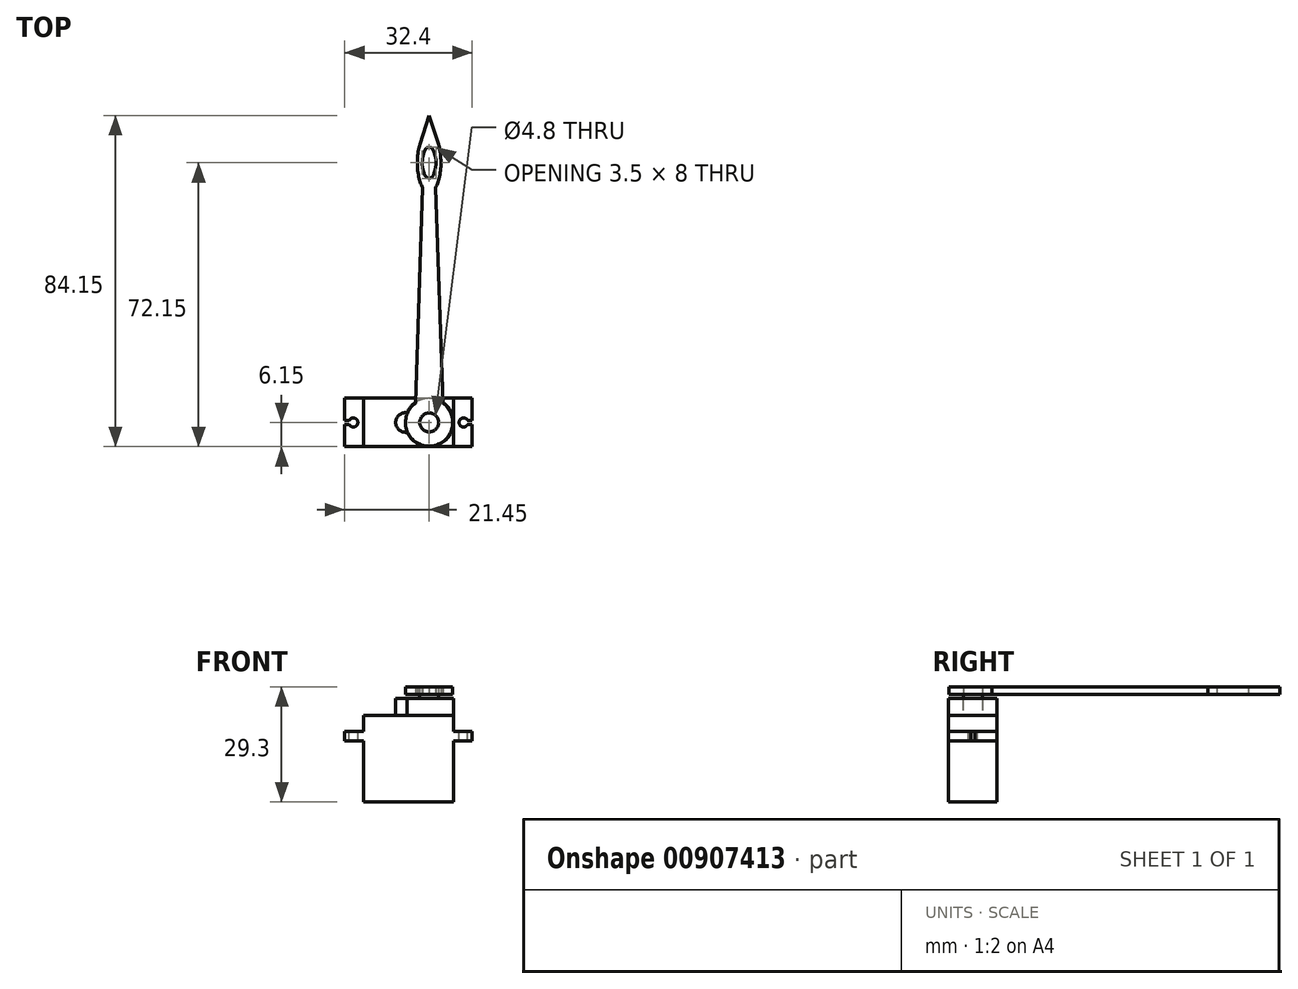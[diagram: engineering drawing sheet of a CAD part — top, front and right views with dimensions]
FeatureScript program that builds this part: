
annotation { "Feature Type Name" : "Feature", "Feature Type Description" : "" }
export const myFeature = defineFeature(function(context is Context, id is Id, definition is map)
    precondition{}
    {
        {
            var Q0;
            Q0=qCreatedBy(makeId("Top.planeOp"),FACE);
            var sketch = newSketch(context, id + "F0", { "sketchPlane" : qUnion([Q0])});
            skLineSegment(sketch, "E0.bottom", {"start": v(0, 0) * mm, "end": v(22.8, 0) * mm});
            skLineSegment(sketch, "E0.top", {"start": v(0, 12.3) * mm, "end": v(22.8, 12.3) * mm});
            skLineSegment(sketch, "E0.left", {"start": v(0, 0) * mm, "end": v(0, 12.3) * mm});
            skLineSegment(sketch, "E0.right", {"start": v(22.8, 0) * mm, "end": v(22.8, 12.3) * mm});
            skSolve(sketch);
        }
        {
            var Q0;
            Q0=qSketchRegion(id+"F0",true);
            extrude(context, id + "F1", {"entities" : qUnion([Q0]), "depth" : 18 * mm, "offsetDistance" : 25 * mm});
        }
        {
            var Q0;
            Q0=makeQuery(id+"F1.opExtrude","CAP_FACE",FACE,{"disambiguationData":[OSD([sQuery(id+"F0.wireOp",EDGE,"E0.bottom"),sQuery(id+"F0.wireOp",EDGE,"E0.top"),sQuery(id+"F0.wireOp",EDGE,"E0.left"),sQuery(id+"F0.wireOp",EDGE,"E0.right")])],"isStart":false});
            var sketch = newSketch(context, id + "F2", { "sketchPlane" : qUnion([Q0])});
            skLineSegment(sketch, "E1.0", {"start": v(0, 12.3) * mm, "end": v(22.8, 12.3) * mm});
            skLineSegment(sketch, "E2.0", {"start": v(0, 0) * mm, "end": v(22.8, 0) * mm});
            skLineSegment(sketch, "E3", {"start": v(0, 12.3) * mm, "end": v(-4.8, 12.3) * mm});
            skLineSegment(sketch, "E4", {"start": v(-4.8, 12.3) * mm, "end": v(-4.8, 6.65) * mm});
            skLineSegment(sketch, "E5", {"start": v(-4.8, 0) * mm, "end": v(0, 0) * mm});
            skLineSegment(sketch, "E6", {"start": v(22.8, 0) * mm, "end": v(27.6, 0) * mm});
            skLineSegment(sketch, "E7", {"start": v(27.6, 0) * mm, "end": v(27.6, 5.65) * mm});
            skLineSegment(sketch, "E8", {"start": v(27.6, 12.3) * mm, "end": v(22.8, 12.3) * mm});
            skArc(sketch, "E9", {"start": v(-3.64, 5.65) * mm, "mid": v(-1.45, 6.15) * mm, "end": v(-3.64, 6.65) * mm});
            skArc(sketch, "E10", {"start": v(26.44, 6.65) * mm, "mid": v(24.25, 6.15) * mm, "end": v(26.44, 5.65) * mm});
            skPoint(sketch, "E10.centerSnap0", {"position": v(22.8, 6.15) * mm});
            skLineSegment(sketch, "E11", {"start": v(-2.6, 6.15) * mm, "end": v(25.4, 6.15) * mm, "construction": true});
            skLineSegment(sketch, "E12", {"start": v(11.4, 6.15) * mm, "end": v(11.4, 12.3) * mm, "construction": true});
            skLineSegment(sketch, "E13", {"start": v(-4.8, 6.65) * mm, "end": v(-3.64, 6.65) * mm});
            skLineSegment(sketch, "E14", {"start": v(-4.8, 5.65) * mm, "end": v(-3.64, 5.65) * mm});
            skLineSegment(sketch, "E15", {"start": v(26.44, 6.65) * mm, "end": v(27.6, 6.65) * mm});
            skLineSegment(sketch, "E16", {"start": v(26.44, 5.65) * mm, "end": v(27.6, 5.65) * mm});
            skLineSegment(sketch, "E17.trimOffspring", {"start": v(-4.8, 5.65) * mm, "end": v(-4.8, 0) * mm});
            skLineSegment(sketch, "E18.trimOffspring", {"start": v(27.6, 6.65) * mm, "end": v(27.6, 12.3) * mm});
            skSolve(sketch);
        }
        {
            var Q0;
            Q0=qSketchRegion(id+"F2",true);
            extrude(context, id + "F3", {"entities" : qUnion([Q0]), "operationType" : NewBodyOperationType.ADD, "oppositeDirection" : true, "depth" : 2.5 * mm, "offsetDistance" : 25 * mm});
        }
        {
            var Q0;
            Q0=makeQuery(id+"F3.boolean.opBoolean","MERGE",FACE,{"derivedFrom":[makeQuery(id+"F1.opExtrude","CAP_FACE",FACE,{"disambiguationData":[OSD([sQuery(id+"F0.wireOp",EDGE,"E0.bottom"),sQuery(id+"F0.wireOp",EDGE,"E0.top"),sQuery(id+"F0.wireOp",EDGE,"E0.left"),sQuery(id+"F0.wireOp",EDGE,"E0.right")])],"isStart":false}),makeQuery(id+"F3.opExtrude","CAP_FACE",FACE,{"disambiguationData":[OSD([sQuery(id+"F2.wireOp",EDGE,"E1.0"),sQuery(id+"F2.wireOp",EDGE,"E2.0"),sQuery(id+"F2.wireOp",EDGE,"E3"),sQuery(id+"F2.wireOp",EDGE,"E4"),sQuery(id+"F2.wireOp",EDGE,"E5"),sQuery(id+"F2.wireOp",EDGE,"E6"),sQuery(id+"F2.wireOp",EDGE,"E7"),sQuery(id+"F2.wireOp",EDGE,"E8"),sQuery(id+"F2.wireOp",EDGE,"E9"),sQuery(id+"F2.wireOp",EDGE,"E10")])],"isStart":true})]});
            var sketch = newSketch(context, id + "F4", { "sketchPlane" : qUnion([Q0])});
            skLineSegment(sketch, "E19.0", {"start": v(22.8, 0) * mm, "end": v(22.8, 12.3) * mm});
            skLineSegment(sketch, "E20.0", {"start": v(0, 0) * mm, "end": v(0, 12.3) * mm});
            skSolve(sketch);
        }
        {
            var Q0;
            {var subQ0=sQuery(id+"F4.wireOp",EDGE,"E19.0");Q0=makeQuery(id+"F4.imprint","IMPRINT",FACE,{"disambiguationData":[TD([[makeQuery(id+"F4.imprint","IMPRINT",EDGE,{"derivedFrom":subQ0}),1.0]])]});}
            extrude(context, id + "F5", {"entities" : qUnion([Q0]), "operationType" : NewBodyOperationType.ADD, "depth" : 4 * mm, "offsetDistance" : 25 * mm});
        }
        {
            var Q0;
            Q0=makeQuery(id+"F5.opExtrude","CAP_FACE",FACE,{"disambiguationData":[OSD([sQuery(id+"F0.wireOp",EDGE,"E0.bottom"),sQuery(id+"F0.wireOp",EDGE,"E0.top"),sQuery(id+"F2.wireOp",EDGE,"E1.0"),sQuery(id+"F2.wireOp",EDGE,"E2.0"),sQuery(id+"F2.wireOp",EDGE,"E3"),sQuery(id+"F2.wireOp",EDGE,"E5"),sQuery(id+"F2.wireOp",EDGE,"E6"),sQuery(id+"F2.wireOp",EDGE,"E8"),sQuery(id+"F4.wireOp",EDGE,"E19.0"),sQuery(id+"F4.wireOp",EDGE,"E20.0")])],"isStart":false});
            var sketch = newSketch(context, id + "F6", { "sketchPlane" : qUnion([Q0])});
            skArc(sketch, "E21", {"start": v(11.03, 3.65) * mm, "mid": v(22.8, 6.15) * mm, "end": v(11.03, 8.65) * mm});
            skPoint(sketch, "E21.first.point", {"position": v(16.65, 0) * mm});
            skPoint(sketch, "E21.second.point", {"position": v(22.8, 6.15) * mm});
            skPoint(sketch, "E21.third.point", {"position": v(16.65, 12.3) * mm});
            skArc(sketch, "E22", {"start": v(10.65, 8.65) * mm, "mid": v(8.15, 6.15) * mm, "end": v(10.65, 3.65) * mm});
            skLineSegment(sketch, "E23", {"start": v(10.65, 8.65) * mm, "end": v(11.03, 8.65) * mm});
            skLineSegment(sketch, "E24", {"start": v(10.65, 3.65) * mm, "end": v(11.03, 3.65) * mm});
            skSolve(sketch);
        }
        {
            var Q0;
            Q0=qSketchRegion(id+"F6",true);
            extrude(context, id + "F7", {"entities" : qUnion([Q0]), "operationType" : NewBodyOperationType.ADD, "depth" : 4.3 * mm, "offsetDistance" : 25 * mm});
        }
        {
            var Q0;
            Q0=makeQuery(id+"F7.opExtrude","CAP_FACE",FACE,{"disambiguationData":[OSD([sQuery(id+"F6.wireOp",EDGE,"E21"),sQuery(id+"F6.wireOp",EDGE,"E22"),sQuery(id+"F6.wireOp",EDGE,"E23"),sQuery(id+"F6.wireOp",EDGE,"E24")])],"isStart":false});
            var sketch = newSketch(context, id + "F8", { "sketchPlane" : qUnion([Q0])});
            skCircle(sketch, "E25", {"center": v(16.65, 6.15) * mm, "radius": 2.4 * mm});
            skSolve(sketch);
        }
        {
            var Q0;
            Q0=qSketchRegion(id+"F8",true);
            extrude(context, id + "F9", {"entities" : qUnion([Q0]), "operationType" : NewBodyOperationType.ADD, "depth" : 2.9 * mm, "offsetDistance" : 25 * mm});
        }
        {
            var Q0;
            Q0=makeQuery(id+"F7.opExtrude","CAP_FACE",FACE,{"disambiguationData":[OSD([sQuery(id+"F6.wireOp",EDGE,"E21"),sQuery(id+"F6.wireOp",EDGE,"E22"),sQuery(id+"F6.wireOp",EDGE,"E23"),sQuery(id+"F6.wireOp",EDGE,"E24")])],"isStart":false});
            cPlane(context, id + "F10", {"entities" : qUnion([Q0]), "cplaneType" : CPlaneType.OFFSET, "offset" : 1 * mm, "width" : 150 * mm, "height" : 150 * mm});
        }
        {
            var Q0;
            Q0=qCreatedBy(id+"F10.planeOp",FACE);
            var sketch = newSketch(context, id + "F11", { "sketchPlane" : qUnion([Q0])});
            skCircle(sketch, "E26.0", {"center": v(16.65, 6.15) * mm, "radius": 2.4 * mm, "construction": true});
            skCircle(sketch, "E27", {"center": v(16.65, 6.15) * mm, "radius": 6 * mm});
            skCircle(sketch, "E28", {"center": v(16.65, 6.15) * mm, "radius": 2.4 * mm});
            skLineSegment(sketch, "E29", {"start": v(13.15, 11.02) * mm, "end": v(15.04, 65.83) * mm});
            skLineSegment(sketch, "E30", {"start": v(15.15, 69.15) * mm, "end": v(18.15, 69.15) * mm, "construction": true});
            skLineSegment(sketch, "E31", {"start": v(18.26, 65.83) * mm, "end": v(20.15, 11.02) * mm});
            skLineSegment(sketch, "E32", {"start": v(16.65, 69.15) * mm, "end": v(16.65, 6.15) * mm, "construction": true});
            skEllipticalArc(sketch, "E33", {});
            skLineSegment(sketch, "E34", {"start": v(14.3, 76.84) * mm, "end": v(16.65, 84.15) * mm});
            skLineSegment(sketch, "E35", {"start": v(16.65, 84.15) * mm, "end": v(19, 76.84) * mm});
            skLineSegment(sketch, "E36", {"start": v(16.65, 84.15) * mm, "end": v(16.65, 69.15) * mm, "construction": true});
            skEllipse(sketch, "E37", {"center": v(16.65, 72.15) * mm, "majorRadius": 4 * mm, "minorRadius": 1.75 * mm, "majorAxis": v(0, 1)});
            skEllipticalArc(sketch, "E38.trimOffspring", {});
            const initialGuessF11  = {"E33": [0.01665, 0.07215, 0, -1, 0.0075, 0.003, 4.037257447447658, 5.715008225795697], "E38.trimOffspring": [0.01665, 0.07215, 0, -1, 0.0075, 0.003, 0.5681770813838886, 2.245927859731928]};
            skSetInitialGuess(sketch, initialGuessF11);
            skSolve(sketch);
        }
        {
            var Q0;
            Q0=qSketchRegion(id+"F11",true);
            extrude(context, id + "F12", {"entities" : qUnion([Q0]), "depth" : 2 * mm, "offsetDistance" : 25 * mm});
        }
    });
